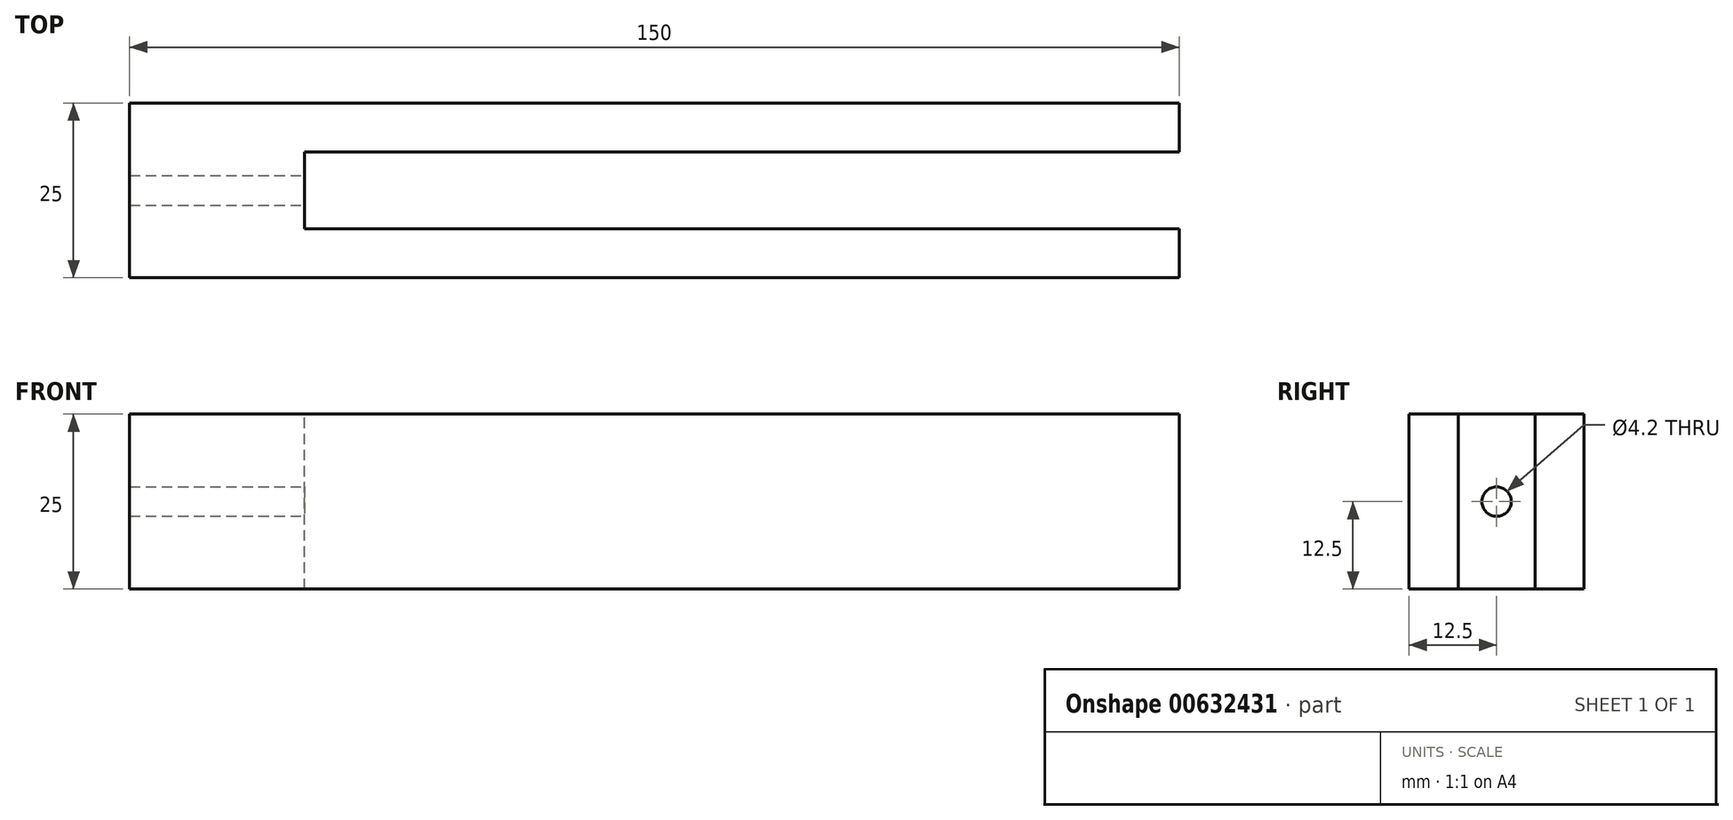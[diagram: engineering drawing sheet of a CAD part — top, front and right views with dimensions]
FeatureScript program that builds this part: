
annotation { "Feature Type Name" : "Feature", "Feature Type Description" : "" }
export const myFeature = defineFeature(function(context is Context, id is Id, definition is map)
    precondition{}
    {
        {
            var Q0;
            Q0=qCreatedBy(makeId("Front.planeOp"),FACE);
            var sketch = newSketch(context, id + "F0", { "sketchPlane" : qUnion([Q0])});
            skLineSegment(sketch, "E0.bottom", {"start": v(0, 0) * mm, "end": v(150, 0) * mm});
            skLineSegment(sketch, "E0.top", {"start": v(0, 25) * mm, "end": v(150, 25) * mm});
            skLineSegment(sketch, "E0.left", {"start": v(0, 0) * mm, "end": v(0, 25) * mm});
            skLineSegment(sketch, "E0.right", {"start": v(150, 0) * mm, "end": v(150, 25) * mm});
            skSolve(sketch);
        }
        {
            var Q0;
            Q0=makeQuery(id+"F0.imprint","IMPRINT",FACE,{"disambiguationData":[TD([[makeQuery(id+"F0.imprint","IMPRINT",EDGE,{"derivedFrom":sQuery(id+"F0.wireOp",EDGE,"E0.bottom")}),1.0]])]});
            extrude(context, id + "F1", {"entities" : qUnion([Q0]), "oppositeDirection" : true, "depth" : 25 * mm, "offsetDistance" : 25 * mm});
        }
        {
            var Q0;
            Q0=makeQuery(id+"F1.opExtrude","SWEPT_FACE",FACE,{"disambiguationData":[OSD([sQuery(id+"F0.wireOp",EDGE,"E0.top")])]});
            var sketch = newSketch(context, id + "F2", { "sketchPlane" : qUnion([Q0])});
            skLineSegment(sketch, "E1.bottom", {"start": v(25, 18) * mm, "end": v(150, 18) * mm});
            skLineSegment(sketch, "E1.top", {"start": v(25, 7) * mm, "end": v(150, 7) * mm});
            skLineSegment(sketch, "E1.left", {"start": v(25, 18) * mm, "end": v(25, 7) * mm});
            skLineSegment(sketch, "E1.right", {"start": v(150, 18) * mm, "end": v(150, 7) * mm});
            skSolve(sketch);
        }
        {
            var Q0;
            Q0=makeQuery(id+"F2.imprint","IMPRINT",FACE,{"disambiguationData":[TD([[makeQuery(id+"F2.imprint","IMPRINT",EDGE,{"derivedFrom":sQuery(id+"F2.wireOp",EDGE,"E1.bottom")}),-1.0]])]});
            extrude(context, id + "F3", {"entities" : qUnion([Q0]), "operationType" : NewBodyOperationType.REMOVE, "endBound" : BoundingType.THROUGH_ALL, "oppositeDirection" : true, "depth" : 25 * mm, "offsetDistance" : 25 * mm});
        }
        {
            var Q0;
            Q0=makeQuery(id+"F1.opExtrude","SWEPT_FACE",FACE,{"disambiguationData":[OSD([sQuery(id+"F0.wireOp",EDGE,"E0.left")])]});
            var sketch = newSketch(context, id + "F4", { "sketchPlane" : qUnion([Q0])});
            skPoint(sketch, "E2", {"position": v(-12.5, 12.5) * mm});
            skPoint(sketch, "E2.positionSnap0", {"position": v(-12.5, 25) * mm});
            skPoint(sketch, "E2.positionSnap1", {"position": v(-25, 12.5) * mm});
            skSolve(sketch);
        }
        {
            var Q0;
            Q0=sQuery(id+"F4.wireOp",VERTEX,"E2");
            var Q1;
            Q1=makeQuery(id+"F1.opExtrude","SWEPT_BODY",BODY,{"disambiguationData":[OSD([sQuery(id+"F0.wireOp",EDGE,"E0.bottom"),sQuery(id+"F0.wireOp",EDGE,"E0.top"),sQuery(id+"F0.wireOp",EDGE,"E0.left"),sQuery(id+"F0.wireOp",EDGE,"E0.right")])]});
            hole(context, id + "F5", {"style" : HoleStyle.SIMPLE, "endStyle" : HoleEndStyle.THROUGH, "standardTappedOrClearance" : lookupTablePath({ "standard" : "ISO", "engagement" : "75%", "pitch" : "0.8 mm", "size" : "M5", "type" : "Tapped" }), "standardBlindInLast" : lookupTablePath({ "standard" : "ISO", "engagement" : "75%", "pitch" : "0.8 mm", "size" : "M5", "type" : "Tapped" }), "holeDiameter" : 4.2 * mm, "majorDiameter" : 5 * mm, "showTappedDepth" : true, "isTappedThrough" : true, "tappedDepth" : 12 * mm, "tapClearance" : 3, "startFromSketch" : true, "locations" : qUnion([Q0]), "scope" : qUnion([Q1])});
        }
    });
